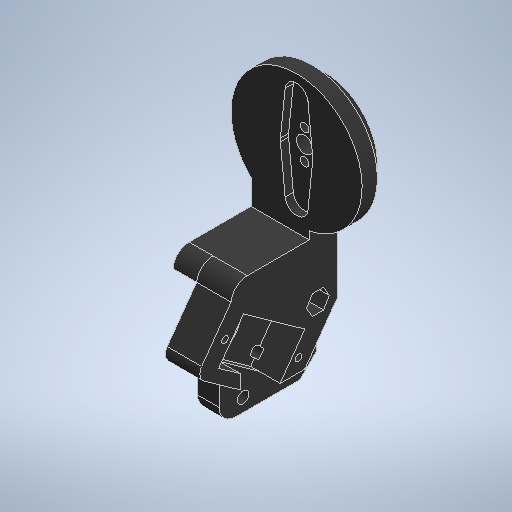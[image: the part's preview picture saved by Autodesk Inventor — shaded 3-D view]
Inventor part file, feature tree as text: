
AUTODESK INVENTOR PART (.ipt)
format: ipt  version: 2025.1 (Build 291241020, 241B)  size: 549,376 bytes
history: native  units: mm
features: extrude x18, sketch x12, chamfer x3, fillet x2, projected_geometry x1
ambient origin geometry x8: Origin, YZ Plane, XZ Plane, XY Plane, X Axis, Y Axis, Z Axis, Center Point
bodies: Body1 (feature_tree)
feature tree (36):
  extrude  "Extrusion48"  Depth=8.65mm TaperAngle=0.0deg
  sketch  "Sketch49"  dims[d338=5.0mm d339=9.0mm]
  extrude  "Extrusion52"  Depth=5.0mm
  extrude  "Extrusion53"  Depth=8.65mm TaperAngle=0.0deg
  extrude  "Extrusion54"  Depth=28.0mm
  extrude  "Extrusion55"  Depth=2.5mm TaperAngle=0.0deg
  extrude  "Extrusion56"  Depth=3.0mm TaperAngle=0.0deg
  sketch  "Sketch55"  dims[d348=6.0mm d349=3.0mm d350=0.0mm]
  extrude  "Extrusion57"  Depth=5.0mm
  extrude  "Extrusion58"  Depth=22.0mm
  extrude  "Extrusion59"  Depth=40.5mm TaperAngle=0.0deg
  sketch  "Sketch56"  dims[d354=17.75mm d355=5.0mm]
  extrude  "Extrusion60"  Depth=10.0mm TaperAngle=0.0deg
  extrude  "Extrusion61"  Depth=3.0mm
  sketch  "Sketch57"  dims[d357=64.0mm d358=22.0mm]
  extrude  "Extrusion62"  Depth=5.0mm
  extrude  "Extrusion63"  Depth=5.0mm
  extrude  "Extrusion64"  Depth=5.0mm
  sketch  "Sketch59"  dims[d363=3.0mm d367=10.0mm d368=0.0mm]
  extrude  "Extrusion65"  Depth=5.0mm
  extrude  "Extrusion66"  Depth=5.0mm
  extrude  "Extrusion67"  Depth=5.0mm
  extrude  "Extrusion68"  Depth=5.0mm
  chamfer  "Chamfer5"  Distance=2.0mm
  chamfer  "Chamfer6"  Distance=24.0mm
  fillet  "Fillet12"  Radius=28.3616mm
  fillet  "Fillet13"  Radius=20.0mm
  chamfer  "Chamfer7"  Distance=7.25mm
  sketch  "Sketch45"  dims[d321=40.0mm d322=8.65mm d323=0.0mm]
  sketch  "Sketch50"  dims[d340=2.6mm d341=8.65mm d342=0.0mm]
  sketch  "Sketch52"  dims[d343=7.0mm d344=28.0mm]
  sketch  "Sketch54"  dims[d345=9.9mm d346=2.5mm d347=0.0mm]
  sketch  "Sketch58"  dims[d359=40.5mm d360=0.0mm d361=40.5mm d362=0.0mm]
  sketch  "Sketch60"  dims[d369=23.0mm d370=3.0mm]
  projected_geometry  "Projected Loop9"
  sketch  "Sketch61"  dims[d371=6.0mm d372=0.5mm d375=38.0mm d377=12.0mm d378=1.5mm d383=1.5mm d384=3.5mm d385=1.0mm d386=2.0mm d388=24.0mm d389=28.3616mm d392=20.0mm d393=7.25mm d394=0.0mm d395=0.0mm d396=0.0mm d397=32.5mm d398=25.2mm d399=3.0mm d400=21.9mm d402=15.0mm d403=0.0mm d404=0.0mm d405=10.0mm d406=0.0mm d407=3.5mm d408=14.0mm d409=60.0mm d410=18.0mm d413=3.3mm d414=13.0mm d415=45.0deg d416=4.65mm d417=0.0mm d418=0.0mm d419=0.0mm d420=6.0mm d421=6.5mm d422=0.0mm d423=13.0mm d424=23.0mm d427=2.3mm d428=2.0mm d429=3.5mm d430=6.0mm d431=9.0mm d432=0.0mm d433=10.0mm d434=0.0mm d437=13.0mm d438=0.0mm d439=0.0mm d440=6.5mm d441=0.0mm d442=1.0mm d443=2.0mm d444=45.0deg d445=5.0mm d446=2.0mm d447=45.0deg d448=5.0mm d449=5.0mm d450=4.0mm d451=2.0mm d452=45.0deg d252=0.0mm d253=0.0mm d254=0.0mm d255=0.0mm]
